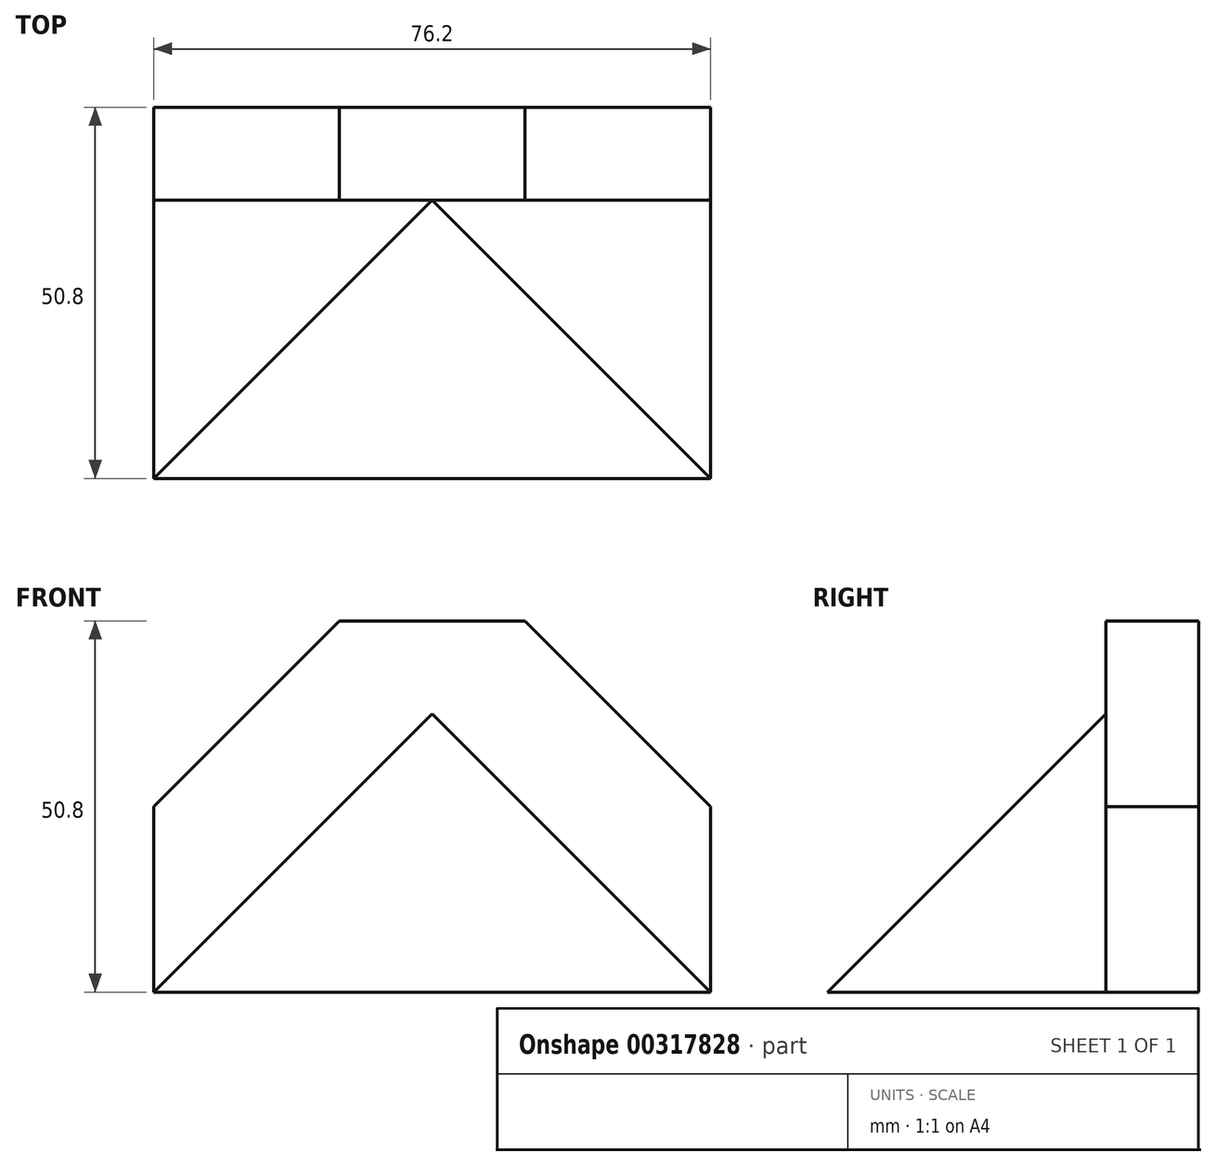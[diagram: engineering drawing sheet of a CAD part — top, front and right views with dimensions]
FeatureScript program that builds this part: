
annotation { "Feature Type Name" : "Feature", "Feature Type Description" : "" }
export const myFeature = defineFeature(function(context is Context, id is Id, definition is map)
    precondition{}
    {
        {
            var Q0;
            Q0=qCreatedBy(makeId("Front.planeOp"),FACE);
            var sketch = newSketch(context, id + "F0", { "sketchPlane" : qUnion([Q0])});
            skLineSegment(sketch, "E0", {"start": v(0, 0) * mm, "end": v(0, 50.8) * mm});
            skLineSegment(sketch, "E1", {"start": v(0, 50.8) * mm, "end": v(76.2, 50.8) * mm});
            skLineSegment(sketch, "E2", {"start": v(76.2, 50.8) * mm, "end": v(76.2, 0) * mm});
            skLineSegment(sketch, "E3", {"start": v(76.2, 0) * mm, "end": v(0, 0) * mm});
            skSolve(sketch);
        }
        {
            var Q0;
            Q0 = qSketchRegion(id + "F0", true);
            extrude(context, id + "F1", {"entities" : qUnion([Q0]), "endBound" : BoundingType.SYMMETRIC, "depth" : 12.7 * mm});
        }
        {
            var Q0;
            Q0=makeQuery(id+"F1.opExtrude","CAP_FACE",FACE,{"disambiguationData":[OSD([sQuery(id+"F0.wireOp",EDGE,"E0"),sQuery(id+"F0.wireOp",EDGE,"E1"),sQuery(id+"F0.wireOp",EDGE,"E2"),sQuery(id+"F0.wireOp",EDGE,"E3")])],"isStart":false});
            var sketch = newSketch(context, id + "F2", { "sketchPlane" : qUnion([Q0])});
            skLineSegment(sketch, "E4", {"start": v(0, 0) * mm, "end": v(76.2, 0) * mm});
            skLineSegment(sketch, "E5", {"start": v(76.2, 0) * mm, "end": v(76.2, 38.1) * mm});
            skLineSegment(sketch, "E6", {"start": v(76.2, 38.1) * mm, "end": v(0, 38.1) * mm});
            skLineSegment(sketch, "E7", {"start": v(0, 38.1) * mm, "end": v(0, 0) * mm});
            skSolve(sketch);
        }
        {
            var Q0;
            Q0 = qSketchRegion(id + "F2", true);
            extrude(context, id + "F3", {"entities" : qUnion([Q0]), "operationType" : NewBodyOperationType.ADD, "depth" : 38.1 * mm});
        }
        {
            var Q0;
            Q0=makeQuery(id+"F3.opExtrude","CAP_FACE",FACE,{"disambiguationData":[OSD([sQuery(id+"F2.wireOp",EDGE,"E4"),sQuery(id+"F2.wireOp",EDGE,"E5"),sQuery(id+"F2.wireOp",EDGE,"E6"),sQuery(id+"F2.wireOp",EDGE,"E7")])],"isStart":false});
            var sketch = newSketch(context, id + "F4", { "sketchPlane" : qUnion([Q0])});
            skLineSegment(sketch, "E8", {"start": v(0, 0) * mm, "end": v(38.1, 38.1) * mm});
            skLineSegment(sketch, "E9", {"start": v(38.1, 38.1) * mm, "end": v(76.2, 0) * mm});
            skLineSegment(sketch, "E10", {"start": v(76.2, 0) * mm, "end": v(57.15, 0) * mm});
            skLineSegment(sketch, "E11", {"start": v(57.15, 0) * mm, "end": v(57.15, 12.7) * mm});
            skLineSegment(sketch, "E12", {"start": v(0, 0) * mm, "end": v(19.05, 0) * mm});
            skLineSegment(sketch, "E13", {"start": v(19.05, 0) * mm, "end": v(19.05, 12.7) * mm});
            skLineSegment(sketch, "E14", {"start": v(19.05, 12.7) * mm, "end": v(57.15, 12.7) * mm});
            skSolve(sketch);
        }
        {
            var Q0;
            {var subQ0=sQuery(id+"F4.wireOp",EDGE,"E8");Q0=makeQuery(id+"F4.imprint","IMPRINT",FACE,{"disambiguationData":[TD([[makeQuery(id+"F4.imprint","IMPRINT",EDGE,{"derivedFrom":subQ0}),1.0]])]});}
            var Q1;
            {var subQ0=sQuery(id+"F4.wireOp",EDGE,"E9");Q1=makeQuery(id+"F4.imprint","IMPRINT",FACE,{"disambiguationData":[TD([[makeQuery(id+"F4.imprint","IMPRINT",EDGE,{"derivedFrom":subQ0}),1.0]])]});}
            extrude(context, id + "F5", {"entities" : qUnion([Q0, Q1]), "operationType" : NewBodyOperationType.REMOVE, "oppositeDirection" : true, "depth" : 38.1 * mm});
        }
        {
            var Q0;
            Q0=qCreatedBy(makeId("Right.planeOp"),FACE);
            var sketch = newSketch(context, id + "F6", { "sketchPlane" : qUnion([Q0])});
            skLineSegment(sketch, "E15", {"start": v(-6.35, 38.1) * mm, "end": v(-44.45, 0) * mm});
            skLineSegment(sketch, "E16", {"start": v(-44.45, 0) * mm, "end": v(-44.45, 38.1) * mm});
            skLineSegment(sketch, "E17", {"start": v(-44.45, 38.1) * mm, "end": v(-6.35, 38.1) * mm});
            skSolve(sketch);
        }
        {
            var Q0;
            Q0 = qSketchRegion(id + "F6", true);
            extrude(context, id + "F7", {"entities" : qUnion([Q0]), "operationType" : NewBodyOperationType.REMOVE, "endBound" : BoundingType.THROUGH_ALL, "depth" : 25.4 * mm});
        }
        {
            var Q0;
            Q0=makeQuery(id+"F1.opExtrude","CAP_FACE",FACE,{"disambiguationData":[OSD([sQuery(id+"F0.wireOp",EDGE,"E0"),sQuery(id+"F0.wireOp",EDGE,"E1"),sQuery(id+"F0.wireOp",EDGE,"E2"),sQuery(id+"F0.wireOp",EDGE,"E3")])],"isStart":true});
            var sketch = newSketch(context, id + "F8", { "sketchPlane" : qUnion([Q0])});
            skLineSegment(sketch, "E18", {"start": v(-76.2, 0) * mm, "end": v(-76.2, 25.4) * mm});
            skLineSegment(sketch, "E19", {"start": v(-38.1, 50.8) * mm, "end": v(-38.1, -15.79) * mm, "construction": true});
            skLineSegment(sketch, "E20", {"start": v(-76.2, 0) * mm, "end": v(-38.1, 0) * mm});
            skLineSegment(sketch, "E21", {"start": v(-38.1, 50.8) * mm, "end": v(-50.8, 50.8) * mm});
            skLineSegment(sketch, "E22", {"start": v(-76.2, 25.4) * mm, "end": v(-50.8, 50.8) * mm});
            skLineSegment(sketch, "E23.MirrorCS", {"start": v(0, 0) * mm, "end": v(-38.1, 0) * mm});
            skLineSegment(sketch, "E24.MirrorCS", {"start": v(0, 0) * mm, "end": v(0, 25.4) * mm});
            skLineSegment(sketch, "E25.MirrorCS", {"start": v(0, 25.4) * mm, "end": v(-25.4, 50.8) * mm});
            skLineSegment(sketch, "E26.MirrorCS", {"start": v(-38.1, 50.8) * mm, "end": v(-25.4, 50.8) * mm});
            skLineSegment(sketch, "E27", {"start": v(-38.1, 0) * mm, "end": v(-57.15, 0) * mm});
            skLineSegment(sketch, "E28", {"start": v(-57.15, 0) * mm, "end": v(-57.15, 12.7) * mm});
            skLineSegment(sketch, "E29", {"start": v(-57.15, 12.7) * mm, "end": v(-38.1, 12.7) * mm});
            skLineSegment(sketch, "E30.MirrorCS", {"start": v(-19.05, 12.7) * mm, "end": v(-38.1, 12.7) * mm});
            skLineSegment(sketch, "E31.MirrorCS", {"start": v(-19.05, 0) * mm, "end": v(-19.05, 12.7) * mm});
            skLineSegment(sketch, "E32.MirrorCS", {"start": v(-38.1, 0) * mm, "end": v(-19.05, 0) * mm});
            skSolve(sketch);
        }
        {
            var Q0;
            {var subQ0=sQuery(id+"F8.wireOp",EDGE,"E25.MirrorCS");Q0=makeQuery(id+"F8.imprint","IMPRINT",FACE,{"disambiguationData":[TD([[makeQuery(id+"F8.imprint","IMPRINT",EDGE,{"derivedFrom":subQ0}),-1.0]])]});}
            var Q1;
            {var subQ0=sQuery(id+"F8.wireOp",EDGE,"E22");Q1=makeQuery(id+"F8.imprint","IMPRINT",FACE,{"disambiguationData":[TD([[makeQuery(id+"F8.imprint","IMPRINT",EDGE,{"derivedFrom":subQ0}),1.0]])]});}
            var Q2;
            Q2=makeQuery(id+"F8.imprint","IMPRINT",FACE,{"disambiguationData":[TD([[makeQuery(id+"F8.imprint","IMPRINT",EDGE,{"derivedFrom":sQuery(id+"F8.wireOp",EDGE,"E27")}),1.0]])]});
            extrude(context, id + "F9", {"entities" : qUnion([Q0, Q1, Q2]), "operationType" : NewBodyOperationType.REMOVE, "endBound" : BoundingType.THROUGH_ALL, "oppositeDirection" : true, "depth" : 25.4 * mm});
        }
    });
